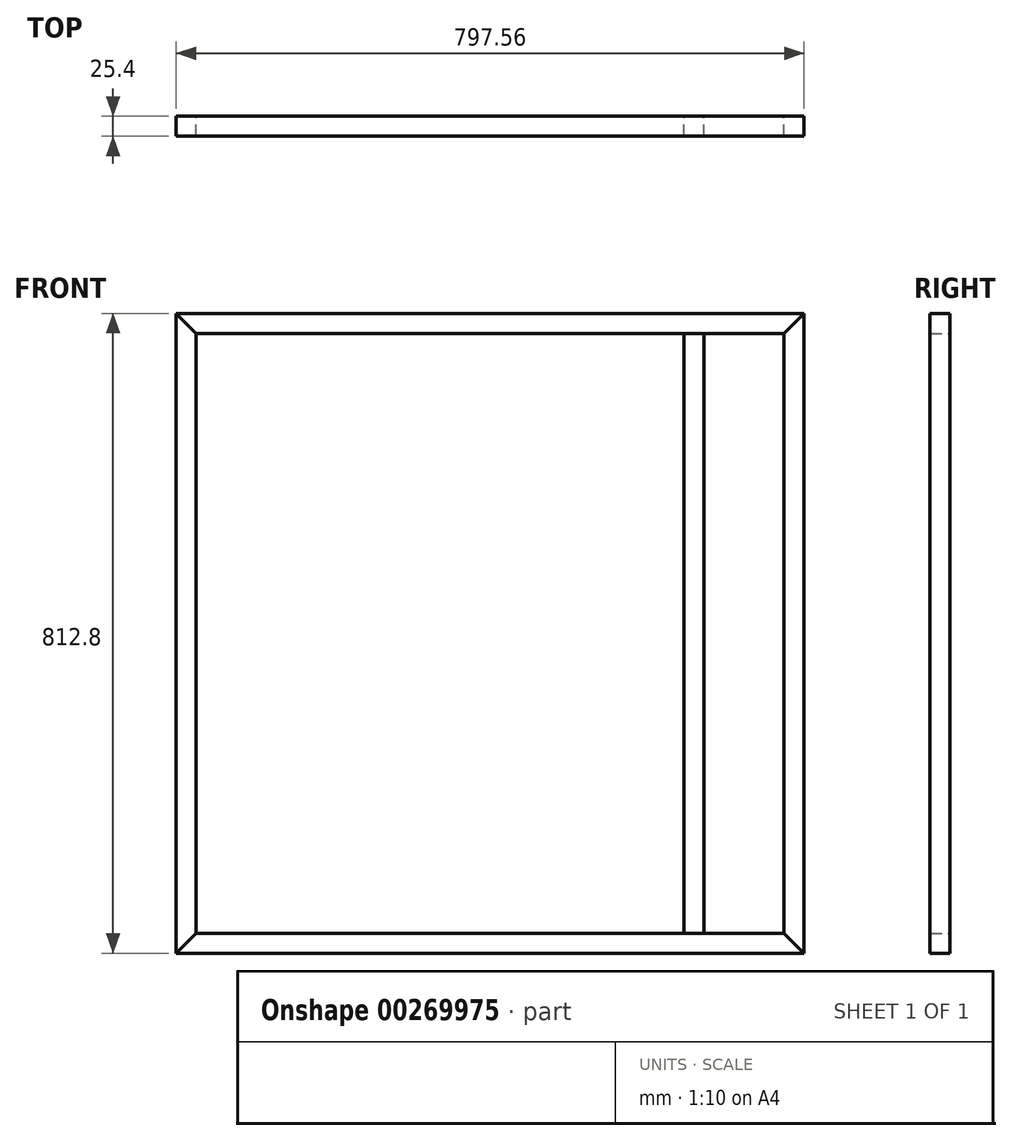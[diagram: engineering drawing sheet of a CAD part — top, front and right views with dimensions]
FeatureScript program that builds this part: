
annotation { "Feature Type Name" : "Feature", "Feature Type Description" : "" }
export const myFeature = defineFeature(function(context is Context, id is Id, definition is map)
    precondition{}
    {
        {
            var Q0;
            Q0=qCreatedBy(makeId("Front.planeOp"),FACE);
            var sketch = newSketch(context, id + "F0", { "sketchPlane" : qUnion([Q0])});
            skLineSegment(sketch, "E0", {"start": v(0, 0) * mm, "end": v(-25.4, -25.4) * mm});
            skLineSegment(sketch, "E1", {"start": v(-25.4, -25.4) * mm, "end": v(-25.4, -787.4) * mm});
            skLineSegment(sketch, "E2", {"start": v(-25.4, -787.4) * mm, "end": v(0, -812.8) * mm});
            skLineSegment(sketch, "E3", {"start": v(0, -812.8) * mm, "end": v(0, 0) * mm});
            skLineSegment(sketch, "E4", {"start": v(0, 0) * mm, "end": v(-797.56, 0) * mm});
            skLineSegment(sketch, "E5", {"start": v(-797.56, 0) * mm, "end": v(-772.16, -25.4) * mm});
            skLineSegment(sketch, "E6", {"start": v(-772.16, -25.4) * mm, "end": v(-25.4, -25.4) * mm});
            skLineSegment(sketch, "E7", {"start": v(-25.4, -787.4) * mm, "end": v(-772.16, -787.4) * mm});
            skLineSegment(sketch, "E8", {"start": v(-772.16, -787.4) * mm, "end": v(-797.56, -812.8) * mm});
            skLineSegment(sketch, "E9", {"start": v(-797.56, -812.8) * mm, "end": v(0, -812.8) * mm});
            skLineSegment(sketch, "E10", {"start": v(-797.56, 0) * mm, "end": v(-797.56, -812.8) * mm});
            skLineSegment(sketch, "E11", {"start": v(-772.16, -25.4) * mm, "end": v(-772.16, -787.4) * mm});
            skLineSegment(sketch, "E12.bottom", {"start": v(-797.56, 0) * mm, "end": v(0, 0) * mm});
            skLineSegment(sketch, "E12.right", {"start": v(0, 0) * mm, "end": v(0, -812.8) * mm});
            skLineSegment(sketch, "E13.bottom", {"start": v(-152.4, -25.4) * mm, "end": v(-127, -25.4) * mm});
            skLineSegment(sketch, "E13.top", {"start": v(-152.4, -787.4) * mm, "end": v(-127, -787.4) * mm});
            skLineSegment(sketch, "E13.left", {"start": v(-152.4, -25.4) * mm, "end": v(-152.4, -787.4) * mm});
            skLineSegment(sketch, "E13.right", {"start": v(-127, -25.4) * mm, "end": v(-127, -787.4) * mm});
            skSolve(sketch);
        }
        {
            var Q0;
            Q0=makeQuery(id+"F0.imprint","IMPRINT",FACE,{"disambiguationData":[TD([[makeQuery(id+"F0.imprint","IMPRINT",EDGE,{"derivedFrom":sQuery(id+"F0.wireOp",EDGE,"E0")}),1.0]])]});
            extrude(context, id + "F1", {"entities" : qUnion([Q0]), "depth" : 25.4 * mm, "offsetDistance" : 25.4 * mm});
        }
        {
            var Q0;
            Q0=makeQuery(id+"F0.imprint","IMPRINT",FACE,{"disambiguationData":[TD([[makeQuery(id+"F0.imprint","IMPRINT",EDGE,{"derivedFrom":sQuery(id+"F0.wireOp",EDGE,"E2")}),-1.0]])]});
            extrude(context, id + "F2", {"entities" : qUnion([Q0]), "depth" : 25.4 * mm, "offsetDistance" : 25.4 * mm});
        }
        {
            var Q0;
            Q0=makeQuery(id+"F0.imprint","IMPRINT",FACE,{"disambiguationData":[TD([[makeQuery(id+"F0.imprint","IMPRINT",EDGE,{"derivedFrom":sQuery(id+"F0.wireOp",EDGE,"E5")}),-1.0]])]});
            extrude(context, id + "F3", {"entities" : qUnion([Q0]), "depth" : 25.4 * mm, "offsetDistance" : 25.4 * mm});
        }
        {
            var Q0;
            Q0=makeQuery(id+"F0.imprint","IMPRINT",FACE,{"disambiguationData":[TD([[makeQuery(id+"F0.imprint","IMPRINT",EDGE,{"derivedFrom":sQuery(id+"F0.wireOp",EDGE,"E0")}),-1.0]])]});
            extrude(context, id + "F4", {"entities" : qUnion([Q0]), "depth" : 25.4 * mm, "offsetDistance" : 25.4 * mm});
        }
        {
            var Q0;
            {var subQ2=sQuery(id+"F0.wireOp",EDGE,"E13.left");Q0=makeQuery(id+"F0.imprint","IMPRINT",FACE,{"disambiguationData":[TD([[makeQuery(id+"F0.imprint","IMPRINT",EDGE,{"derivedFrom":subQ2}),1.0]])]});}
            extrude(context, id + "F5", {"entities" : qUnion([Q0]), "depth" : 25.4 * mm, "offsetDistance" : 25.4 * mm});
        }
    });
